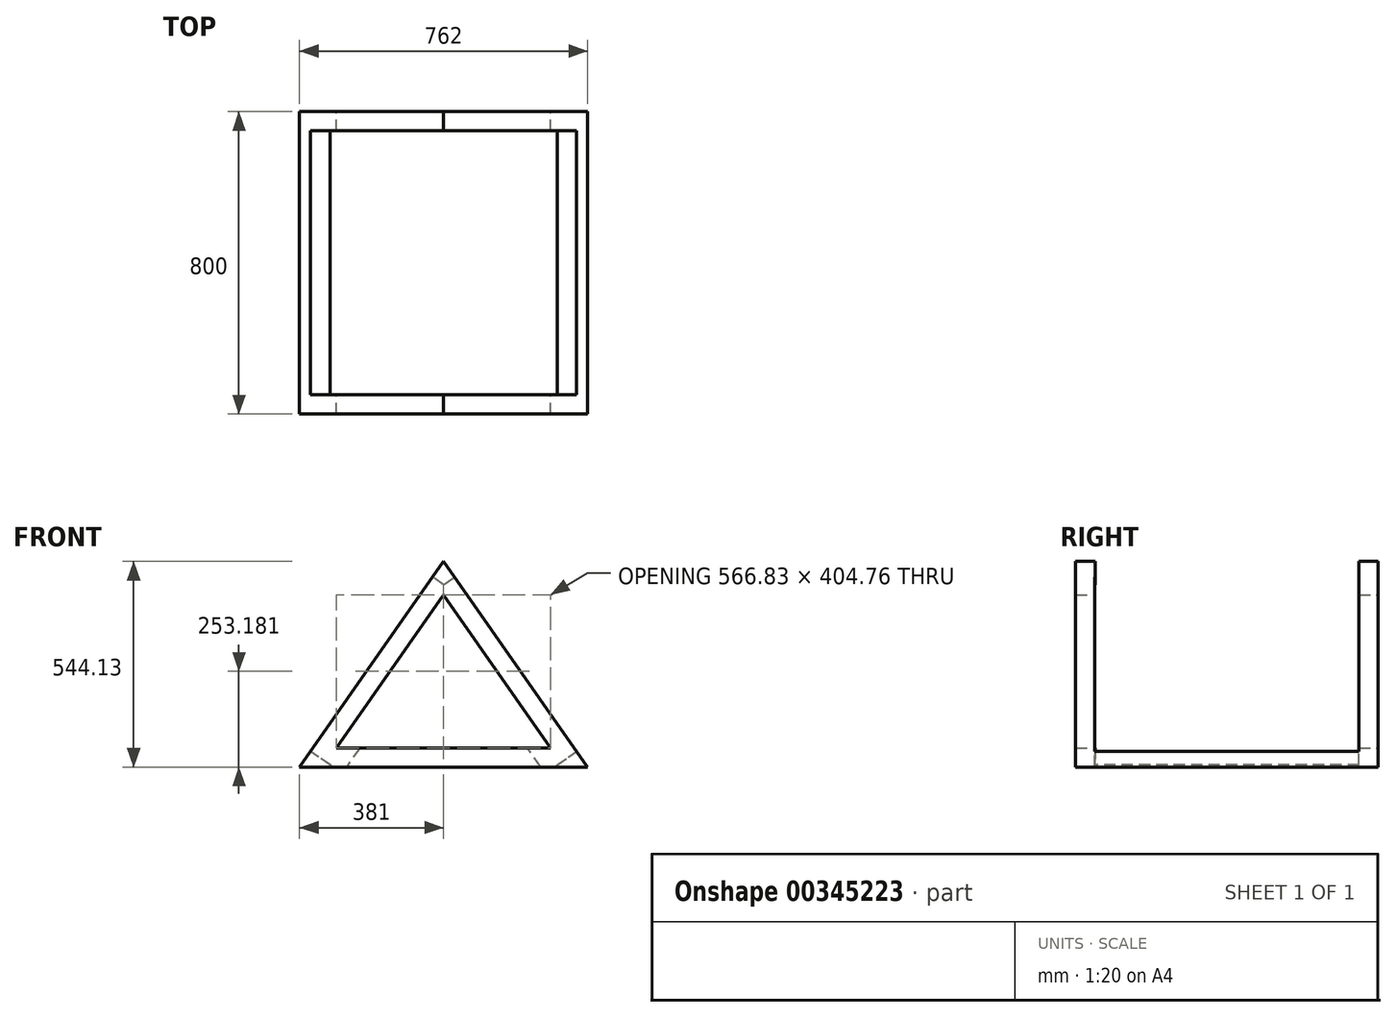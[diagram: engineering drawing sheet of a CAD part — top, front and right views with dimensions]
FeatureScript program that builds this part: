
annotation { "Feature Type Name" : "Feature", "Feature Type Description" : "" }
export const myFeature = defineFeature(function(context is Context, id is Id, definition is map)
    precondition{}
    {
        {
            var Q0;
            Q0=qCreatedBy(makeId("Front.planeOp"),FACE);
            var sketch = newSketch(context, id + "F0", { "sketchPlane" : qUnion([Q0])});
            skLineSegment(sketch, "E0", {"start": v(-381, -275.63) * mm, "end": v(0, 268.5) * mm});
            skLineSegment(sketch, "E1", {"start": v(0, 268.5) * mm, "end": v(381, -275.63) * mm});
            skLineSegment(sketch, "E2", {"start": v(381, -275.63) * mm, "end": v(-381, -275.63) * mm});
            skSolve(sketch);
        }
        {
            var Q0;
            Q0 = qSketchRegion(id + "F0", true);
            extrude(context, id + "F1", {"entities" : qUnion([Q0]), "endBound" : BoundingType.SYMMETRIC, "depth" : 800 * mm});
        }
        {
            var Q0;
            Q0=makeQuery(id+"F1.opExtrude","SWEPT_FACE",FACE,{"disambiguationData":[OSD([sQuery(id+"F0.wireOp",EDGE,"E1")])]});
            var sketch = newSketch(context, id + "F2", { "sketchPlane" : qUnion([Q0])});
            skLineSegment(sketch, "E3.bottom", {"start": v(-349.2, 169.14) * mm, "end": v(349.2, 169.14) * mm});
            skLineSegment(sketch, "E3.top", {"start": v(-349.2, -393.51) * mm, "end": v(349.2, -393.51) * mm});
            skLineSegment(sketch, "E3.left", {"start": v(-349.2, 169.14) * mm, "end": v(-349.2, -393.51) * mm});
            skLineSegment(sketch, "E3.right", {"start": v(349.2, 169.14) * mm, "end": v(349.2, -393.51) * mm});
            skSolve(sketch);
        }
        {
            var Q0;
            Q0 = qSketchRegion(id + "F2", true);
            extrude(context, id + "F3", {"entities" : qUnion([Q0]), "operationType" : NewBodyOperationType.REMOVE, "oppositeDirection" : true, "depth" : 101.6 * mm});
        }
        {
            var Q0;
            Q0=makeQuery(id+"F1.opExtrude","SWEPT_FACE",FACE,{"disambiguationData":[OSD([sQuery(id+"F0.wireOp",EDGE,"E0")])]});
            var sketch = newSketch(context, id + "F4", { "sketchPlane" : qUnion([Q0])});
            skLineSegment(sketch, "E4.bottom", {"start": v(-349.2, -393.51) * mm, "end": v(349.2, -393.51) * mm});
            skLineSegment(sketch, "E4.top", {"start": v(-349.2, 169.14) * mm, "end": v(349.2, 169.14) * mm});
            skLineSegment(sketch, "E4.left", {"start": v(-349.2, -393.51) * mm, "end": v(-349.2, 169.14) * mm});
            skLineSegment(sketch, "E4.right", {"start": v(349.2, -393.51) * mm, "end": v(349.2, 169.14) * mm});
            skSolve(sketch);
        }
        {
            var Q0;
            Q0 = qSketchRegion(id + "F4", true);
            extrude(context, id + "F5", {"entities" : qUnion([Q0]), "operationType" : NewBodyOperationType.REMOVE, "oppositeDirection" : true, "depth" : 101.6 * mm});
        }
        {
            var Q0;
            Q0=makeQuery(id+"F1.opExtrude","CAP_FACE",FACE,{"disambiguationData":[OSD([sQuery(id+"F0.wireOp",EDGE,"E0"),sQuery(id+"F0.wireOp",EDGE,"E1"),sQuery(id+"F0.wireOp",EDGE,"E2")])],"isStart":true});
            var sketch = newSketch(context, id + "F6", { "sketchPlane" : qUnion([Q0])});
            skLineSegment(sketch, "E5", {"start": v(-283.41, -224.83) * mm, "end": v(0, 179.93) * mm});
            skLineSegment(sketch, "E6", {"start": v(0, 179.93) * mm, "end": v(283.41, -224.83) * mm});
            skLineSegment(sketch, "E7", {"start": v(283.41, -224.83) * mm, "end": v(-283.41, -224.83) * mm});
            skSolve(sketch);
        }
        {
            var Q0;
            Q0=makeQuery(id+"F6.imprint","IMPRINT",FACE,{"disambiguationData":[TD([[makeQuery(id+"F6.imprint","IMPRINT",EDGE,{"derivedFrom":sQuery(id+"F6.wireOp",EDGE,"E5")}),-1.0]])]});
            extrude(context, id + "F7", {"entities" : qUnion([Q0]), "operationType" : NewBodyOperationType.REMOVE, "endBound" : BoundingType.THROUGH_ALL, "oppositeDirection" : true, "depth" : 25.4 * mm});
        }
        {
            var Q0;
            Q0=makeQuery(id+"F7.boolean.opBoolean","COPY",FACE,{"derivedFrom":makeQuery(id+"F7.opExtrude","SWEPT_FACE",FACE,{"disambiguationData":[OSD([sQuery(id+"F6.wireOp",EDGE,"E7")])]})});
            var sketch = newSketch(context, id + "F8", { "sketchPlane" : qUnion([Q0])});
            skLineSegment(sketch, "E8.bottom", {"start": v(300, -348.95) * mm, "end": v(-300, -348.95) * mm});
            skLineSegment(sketch, "E8.top", {"start": v(300, 349.2) * mm, "end": v(-300, 349.2) * mm});
            skLineSegment(sketch, "E8.left", {"start": v(300, -348.95) * mm, "end": v(300, 349.2) * mm});
            skLineSegment(sketch, "E8.right", {"start": v(-300, -348.95) * mm, "end": v(-300, 349.2) * mm});
            skSolve(sketch);
        }
        {
            var Q0;
            Q0 = qSketchRegion(id + "F8", true);
            extrude(context, id + "F9", {"entities" : qUnion([Q0]), "operationType" : NewBodyOperationType.REMOVE, "depth" : 584.2 * mm});
        }
        {
            var Q0;
            Q0 = qSketchRegion(id + "F8", true);
            extrude(context, id + "F10", {"entities" : qUnion([Q0]), "operationType" : NewBodyOperationType.REMOVE, "oppositeDirection" : true, "depth" : 101.6 * mm});
        }
    });
